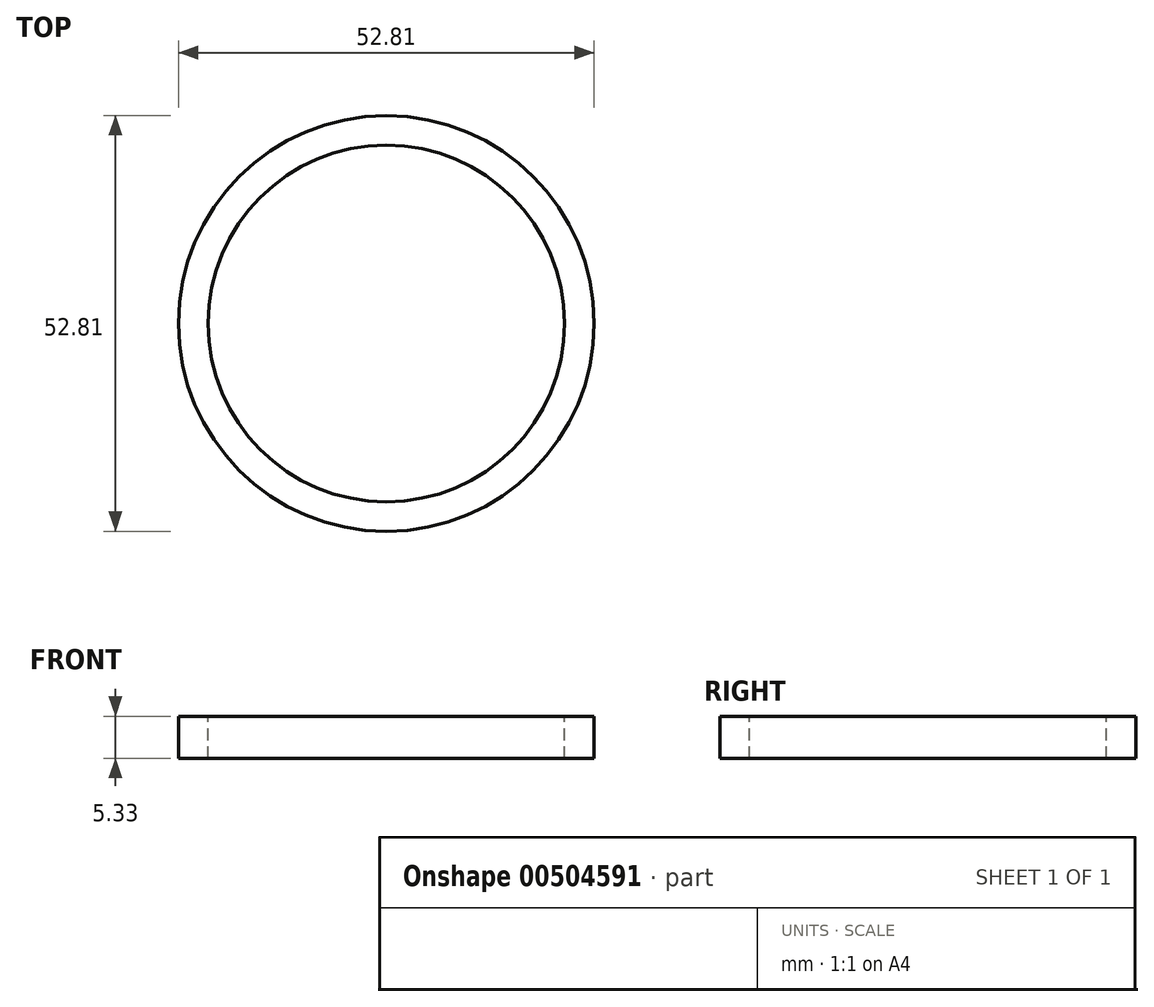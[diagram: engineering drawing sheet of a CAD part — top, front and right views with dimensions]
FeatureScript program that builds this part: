
annotation { "Feature Type Name" : "Feature", "Feature Type Description" : "" }
export const myFeature = defineFeature(function(context is Context, id is Id, definition is map)
    precondition{}
    {
        {
            var Q0;
            Q0=qCreatedBy(makeId("Top.planeOp"),FACE);
            var sketch = newSketch(context, id + "F0", { "sketchPlane" : qUnion([Q0])});
            skCircle(sketch, "E0", {"center": v(-2.38, -2.19) * mm, "radius": 26.4 * mm});
            skCircle(sketch, "E1", {"center": v(-2.38, -2.19) * mm, "radius": 22.65 * mm});
            skCircle(sketch, "E2", {"center": v(-2.38, -2.19) * mm, "radius": 1.26 * mm});
            skSolve(sketch);
        }
        {
            var Q0;
            Q0=sQuery(id+"F0.wireOp",EDGE,"E0");
            var Q1;
            Q1=sQuery(id+"F0.wireOp",EDGE,"E1");
            extrude(context, id + "F1", {"bodyType" : ToolBodyType.SURFACE, "surfaceEntities" : qUnion([Q0, Q1]), "depth" : 5.33 * mm});
        }
    });
